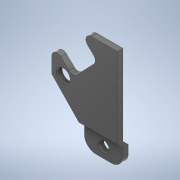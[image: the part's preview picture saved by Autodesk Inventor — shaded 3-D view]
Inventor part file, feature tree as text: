
AUTODESK INVENTOR PART (.ipt)
format: ipt  version: 2020 (Build 240168000, 168)  size: 261,120 bytes
history: native  units: mm
features: extrude x6, sketch x6, fillet x3, chamfer x2, projected_geometry x2
ambient origin geometry x8: Origin, YZ Plane, XZ Plane, XY Plane, X Axis, Y Axis, Z Axis, Center Point
bodies: Solid1 (feature_tree)
feature tree (19):
  extrude  "Extrusion1"  TaperAngle=0.0deg  [1 undecoded]
  extrude  "Extrusion5"  Depth=5.0mm
  fillet  "Fillet2"  Radius=2.5mm
  extrude  "Extrusion6"  Depth=1.0mm
  chamfer  "Chamfer1"  Distance=0.1mm
  extrude  "Extrusion7"  Depth=1.0mm
  chamfer  "Chamfer2"  [1 undecoded]
  extrude  "Extrusion8"  Depth=1.0mm
  extrude  "Extrusion9"  Depth=2.0mm
  fillet  "Fillet3"  Radius=3.525mm
  fillet  "Fillet4"  Radius=2.6mm
  sketch  "Sketch1"  dims[d6=1.0mm d7=0.0mm]
  sketch  "Sketch7"  dims[d26=4.95mm d27=7.25mm d28=2.5mm d29=4.9mm d30=14.9mm d31=5.1mm d32=5.1mm d33=90.0deg d34=135.0deg d36=0.0mm d37=0.0mm]
  projected_geometry  "Projected Loop2"
  sketch  "Sketch8"  dims[d38=2.5mm d39=5.0mm d40=2.5mm]
  sketch  "Sketch9"  dims[d41=1.0mm d42=7.5mm]
  projected_geometry  "Projected Loop3"
  sketch  "Sketch10"  dims[d43=0.15mm]
  sketch  "Sketch11"  dims[d44=0.15mm d54=0.1mm d55=0.1mm d56=0.0mm d57=4.5mm d58=2.0mm d59=3.525mm d60=2.6mm d61=2.0mm d62=0.0mm d63=5.0mm d64=45.0deg d65=5.0mm d66=45.0deg d67=2.1mm d68=0.2mm d69=0.1mm d70=10.0mm d71=0.0mm d72=1.0mm d73=2.0mm d74=45.0deg d75=1.0mm d76=0.0mm d77=1.0mm d78=2.0mm d79=45.0deg d80=3.8mm d81=1.0mm d82=0.0mm d83=7.0mm d85=6.5mm d86=3.5mm d87=1.0mm d88=0.0mm d89=6.5mm d90=1.0mm d91=1.0mm d5=0.5mm d8=0.872665mm d11=0.5mm d12=0.872665mm d13=0.5mm d14=0.872665mm d25=0.5mm]
note: 2 required parameter values undecoded (feature->parameter linkage not recoverable at this tier; creation-order binding heuristic only, values carry confidence <= 0.55)
